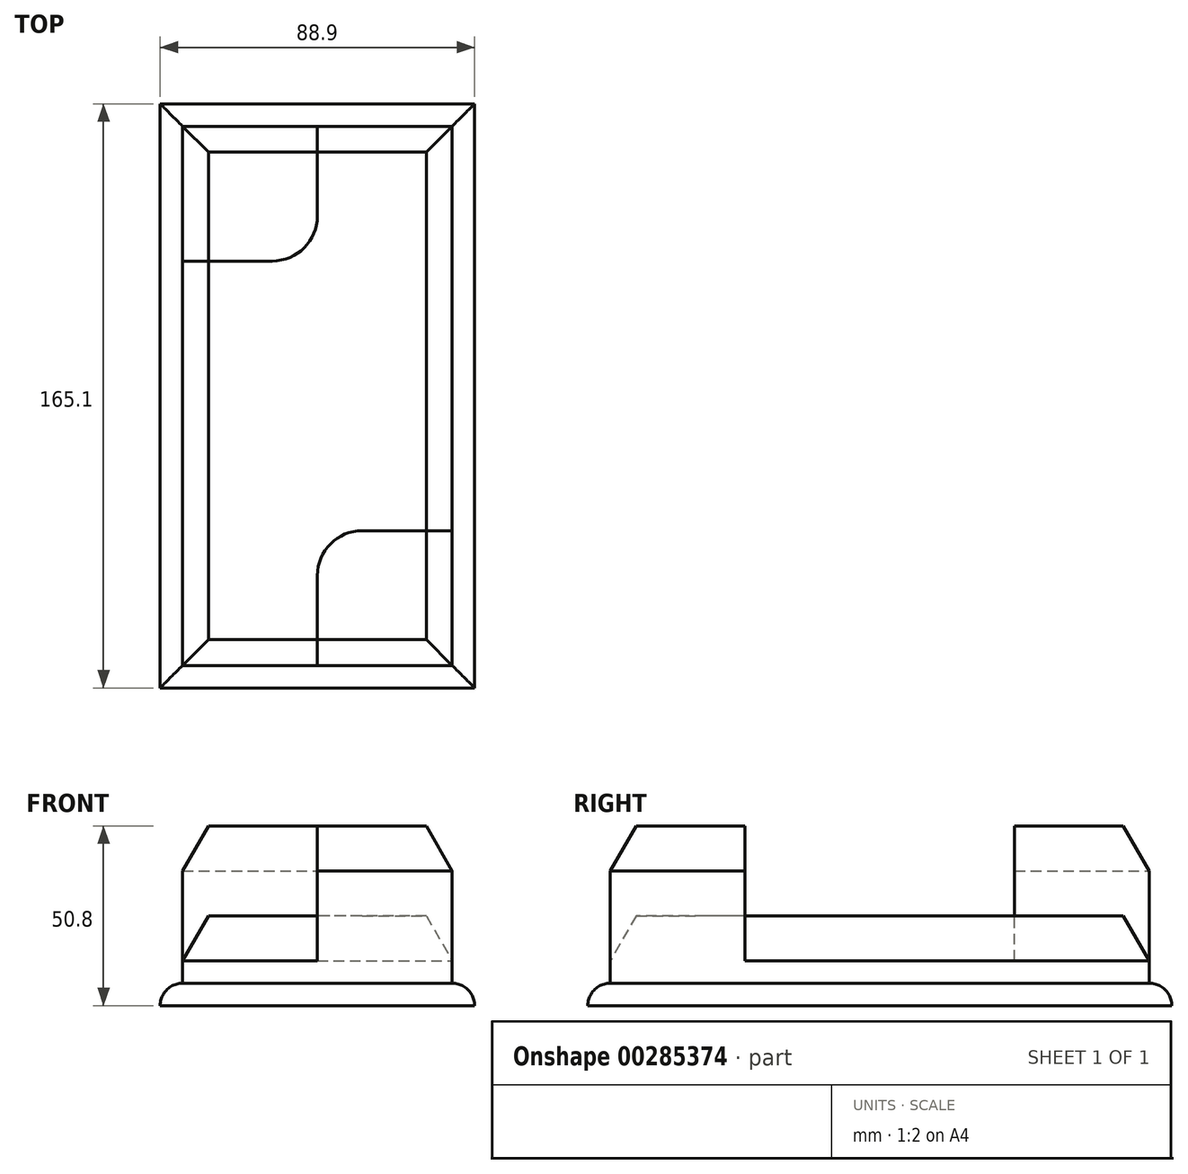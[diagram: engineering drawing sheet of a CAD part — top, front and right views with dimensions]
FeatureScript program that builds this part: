
annotation { "Feature Type Name" : "Feature", "Feature Type Description" : "" }
export const myFeature = defineFeature(function(context is Context, id is Id, definition is map)
    precondition{}
    {
        {
            var Q0;
            Q0=qCreatedBy(makeId("Top.planeOp"),FACE);
            var sketch = newSketch(context, id + "F0", { "sketchPlane" : qUnion([Q0])});
            skLineSegment(sketch, "E0.bottom", {"start": v(-38.1, 76.2) * mm, "end": v(38.1, 76.2) * mm});
            skLineSegment(sketch, "E0.top", {"start": v(-38.1, -76.2) * mm, "end": v(38.1, -76.2) * mm});
            skLineSegment(sketch, "E0.left", {"start": v(-38.1, 76.2) * mm, "end": v(-38.1, -76.2) * mm});
            skLineSegment(sketch, "E0.right", {"start": v(38.1, 76.2) * mm, "end": v(38.1, -76.2) * mm});
            skPoint(sketch, "E0.middle", {"position": v(0, 0) * mm});
            skLineSegment(sketch, "E1.bottom", {"start": v(-44.45, 82.55) * mm, "end": v(44.45, 82.55) * mm});
            skLineSegment(sketch, "E1.top", {"start": v(-44.45, -82.55) * mm, "end": v(44.45, -82.55) * mm});
            skLineSegment(sketch, "E1.left", {"start": v(-44.45, 82.55) * mm, "end": v(-44.45, -82.55) * mm});
            skLineSegment(sketch, "E1.right", {"start": v(44.45, 82.55) * mm, "end": v(44.45, -82.55) * mm});
            skPoint(sketch, "E2", {"position": v(0, 76.2) * mm});
            skLineSegment(sketch, "E3", {"start": v(0, 76.2) * mm, "end": v(0, 50.8) * mm});
            skLineSegment(sketch, "E4", {"start": v(-12.7, 38.1) * mm, "end": v(-38.1, 38.1) * mm});
            skPoint(sketch, "E5.visualSharp", {"position": v(0, 38.1) * mm});
            skArc(sketch, "E5.filletArc", {"start": v(-12.7, 38.1) * mm, "mid": v(-3.72, 41.82) * mm, "end": v(0, 50.8) * mm});
            skLineSegment(sketch, "E6", {"start": v(0, -76.2) * mm, "end": v(0, -50.8) * mm});
            skPoint(sketch, "E6.endSnap0", {"position": v(0, -76.2) * mm});
            skLineSegment(sketch, "E7", {"start": v(12.7, -38.1) * mm, "end": v(38.1, -38.1) * mm});
            skPoint(sketch, "E8.visualSharp", {"position": v(0, -38.1) * mm});
            skArc(sketch, "E8.filletArc", {"start": v(12.7, -38.1) * mm, "mid": v(3.72, -41.82) * mm, "end": v(0, -50.8) * mm});
            skSolve(sketch);
        }
        {
            var Q0;
            Q0=makeQuery(id+"F0.imprint","IMPRINT",FACE,{"disambiguationData":[TD([[makeQuery(id+"F0.imprint","IMPRINT",EDGE,{"derivedFrom":sQuery(id+"F0.wireOp",EDGE,"E1.bottom")}),-1.0]])]});
            extrude(context, id + "F1", {"entities" : qUnion([Q0]), "depth" : 6.35 * mm});
        }
        {
            var Q0;
            {var subQ9=sQuery(id+"F0.wireOp",EDGE,"E3");Q0=makeQuery(id+"F0.imprint","IMPRINT",FACE,{"disambiguationData":[TD([[makeQuery(id+"F0.imprint","IMPRINT",EDGE,{"derivedFrom":subQ9}),1.0]])]});}
            extrude(context, id + "F2", {"entities" : qUnion([Q0]), "operationType" : NewBodyOperationType.ADD, "depth" : 25.4 * mm});
        }
        {
            var Q0;
            {var subQ1=sQuery(id+"F0.wireOp",EDGE,"E3");Q0=makeQuery(id+"F0.imprint","IMPRINT",FACE,{"disambiguationData":[TD([[makeQuery(id+"F0.imprint","IMPRINT",EDGE,{"derivedFrom":subQ1}),-1.0]])]});}
            var Q1;
            {var subQ1=sQuery(id+"F0.wireOp",EDGE,"E6");Q1=makeQuery(id+"F0.imprint","IMPRINT",FACE,{"disambiguationData":[TD([[makeQuery(id+"F0.imprint","IMPRINT",EDGE,{"derivedFrom":subQ1}),-1.0]])]});}
            extrude(context, id + "F3", {"entities" : qUnion([Q0, Q1]), "operationType" : NewBodyOperationType.ADD, "depth" : 50.8 * mm});
        }
        {
            var Q0;
            Q0=makeQuery(id+"F2.opExtrude","CAP_EDGE",EDGE,{"disambiguationData":[OSD([sQuery(id+"F0.wireOp",EDGE,"E0.right")])],"isStart":false});
            var Q1;
            Q1=makeQuery(id+"F2.opExtrude","CAP_EDGE",EDGE,{"disambiguationData":[OSD([sQuery(id+"F0.wireOp",EDGE,"E0.top")])],"isStart":false});
            var Q2;
            Q2=makeQuery(id+"F2.opExtrude","CAP_EDGE",EDGE,{"disambiguationData":[OSD([sQuery(id+"F0.wireOp",EDGE,"E0.left")])],"isStart":false});
            var Q3;
            Q3=makeQuery(id+"F2.opExtrude","CAP_EDGE",EDGE,{"disambiguationData":[OSD([sQuery(id+"F0.wireOp",EDGE,"E0.bottom")])],"isStart":false});
            chamfer(context, id + "F4", {"entities" : qUnion([Q0, Q1, Q2, Q3]), "chamferType" : ChamferType.OFFSET_ANGLE, "width" : 12.7 * mm, "oppositeDirection" : false, "angle" : 30 * degree, "tangentPropagation" : true});
        }
        {
            var Q0;
            Q0=makeQuery(id+"F1.opExtrude","CAP_EDGE",EDGE,{"disambiguationData":[OSD([sQuery(id+"F0.wireOp",EDGE,"E1.bottom")])],"isStart":false});
            var Q1;
            Q1=makeQuery(id+"F1.opExtrude","CAP_EDGE",EDGE,{"disambiguationData":[OSD([sQuery(id+"F0.wireOp",EDGE,"E1.left")])],"isStart":false});
            var Q2;
            Q2=makeQuery(id+"F1.opExtrude","CAP_EDGE",EDGE,{"disambiguationData":[OSD([sQuery(id+"F0.wireOp",EDGE,"E1.right")])],"isStart":false});
            var Q3;
            Q3=makeQuery(id+"F1.opExtrude","CAP_EDGE",EDGE,{"disambiguationData":[OSD([sQuery(id+"F0.wireOp",EDGE,"E1.top")])],"isStart":false});
            fillet(context, id + "F5", {"entities" : qUnion([Q0, Q1, Q2, Q3]), "radius" : 6.35 * mm, "tangentPropagation" : true, "allowEdgeOverflow" : false});
        }
        {
            var Q0;
            Q0=makeQuery(id+"F3.opExtrude","CAP_EDGE",EDGE,{"disambiguationData":[OSD([sQuery(id+"F0.wireOp",EDGE,"E0.top")])],"isStart":false});
            var Q1;
            Q1=makeQuery(id+"F3.opExtrude","CAP_EDGE",EDGE,{"disambiguationData":[OSD([sQuery(id+"F0.wireOp",EDGE,"E0.right")])],"isStart":false});
            chamfer(context, id + "F6", {"entities" : qUnion([Q0, Q1]), "chamferType" : ChamferType.OFFSET_ANGLE, "width" : 12.7 * mm, "oppositeDirection" : true, "angle" : 30 * degree, "tangentPropagation" : true});
        }
        {
            var Q0;
            Q0=makeQuery(id+"F3.opExtrude","CAP_EDGE",EDGE,{"disambiguationData":[OSD([sQuery(id+"F0.wireOp",EDGE,"E0.bottom")])],"isStart":false});
            var Q1;
            Q1=makeQuery(id+"F3.opExtrude","CAP_EDGE",EDGE,{"disambiguationData":[OSD([sQuery(id+"F0.wireOp",EDGE,"E0.left")])],"isStart":false});
            chamfer(context, id + "F7", {"entities" : qUnion([Q0, Q1]), "chamferType" : ChamferType.OFFSET_ANGLE, "width" : 12.7 * mm, "oppositeDirection" : false, "angle" : 30 * degree, "tangentPropagation" : true});
        }
    });
